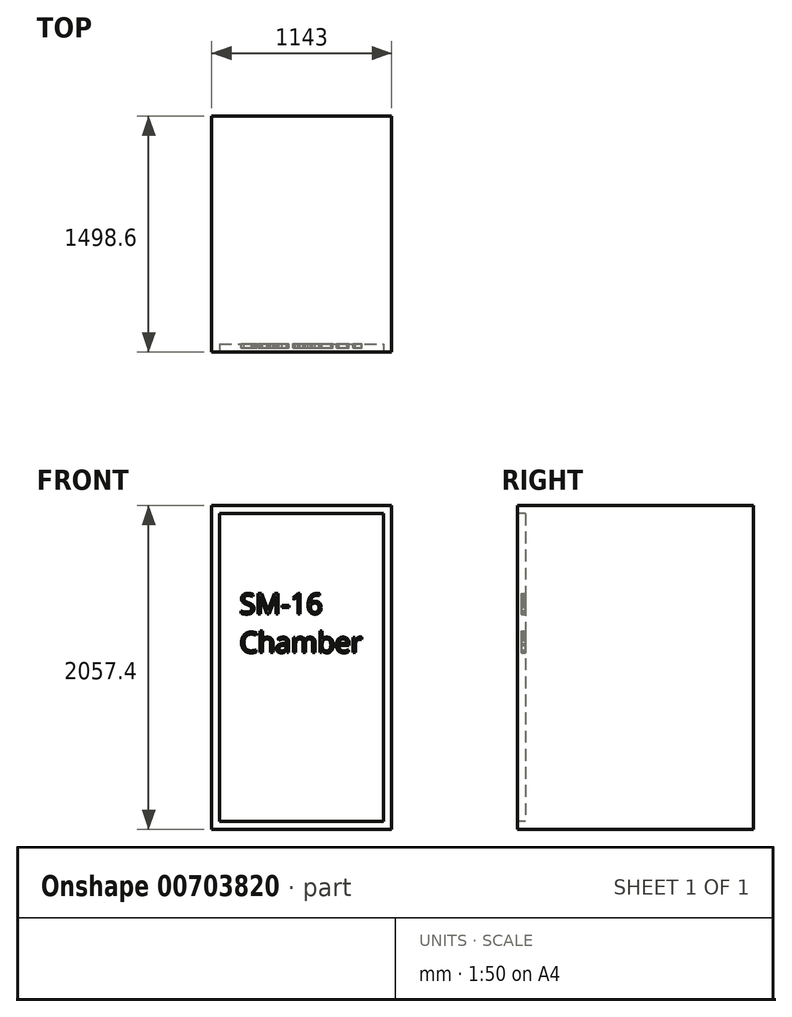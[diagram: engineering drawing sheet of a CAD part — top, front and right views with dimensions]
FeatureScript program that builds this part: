
annotation { "Feature Type Name" : "Feature", "Feature Type Description" : "" }
export const myFeature = defineFeature(function(context is Context, id is Id, definition is map)
    precondition{}
    {
        {
            var Q0;
            Q0=qCreatedBy(makeId("Top.planeOp"),FACE);
            var sketch = newSketch(context, id + "F0", { "sketchPlane" : qUnion([Q0])});
            skLineSegment(sketch, "E0.bottom", {"start": v(571.5, -749.3) * mm, "end": v(-571.5, -749.3) * mm});
            skLineSegment(sketch, "E0.top", {"start": v(571.5, 749.3) * mm, "end": v(-571.5, 749.3) * mm});
            skLineSegment(sketch, "E0.left", {"start": v(571.5, -749.3) * mm, "end": v(571.5, 749.3) * mm});
            skLineSegment(sketch, "E0.right", {"start": v(-571.5, -749.3) * mm, "end": v(-571.5, 749.3) * mm});
            skPoint(sketch, "E0.middle", {"position": v(0, 0) * mm});
            skSolve(sketch);
        }
        {
            var Q0;
            Q0=qSketchRegion(id+"F0",true);
            extrude(context, id + "F1", {"entities" : qUnion([Q0]), "depth" : 2057.4 * mm, "offsetDistance" : 25.4 * mm});
        }
        {
            var Q0;
            Q0=makeQuery(id+"F1.opExtrude","SWEPT_FACE",FACE,{"disambiguationData":[OSD([sQuery(id+"F0.wireOp",EDGE,"E0.bottom")])]});
            var sketch = newSketch(context, id + "F2", { "sketchPlane" : qUnion([Q0])});
            skLineSegment(sketch, "E1.bottom", {"start": v(-520.7, 2006.6) * mm, "end": v(520.7, 2006.6) * mm});
            skLineSegment(sketch, "E1.top", {"start": v(-520.7, 50.8) * mm, "end": v(520.7, 50.8) * mm});
            skLineSegment(sketch, "E1.left", {"start": v(-520.7, 2006.6) * mm, "end": v(-520.7, 50.8) * mm});
            skLineSegment(sketch, "E1.right", {"start": v(520.7, 2006.6) * mm, "end": v(520.7, 50.8) * mm});
            skSolve(sketch);
        }
        {
            var Q0;
            Q0=qSketchRegion(id+"F2",true);
            extrude(context, id + "F3", {"entities" : qUnion([Q0]), "operationType" : NewBodyOperationType.REMOVE, "oppositeDirection" : true, "depth" : 50.8 * mm, "offsetDistance" : 25.4 * mm});
        }
        {
            var Q0;
            Q0=makeQuery(id+"F3.boolean.opBoolean","COPY",FACE,{"derivedFrom":makeQuery(id+"F3.opExtrude","CAP_FACE",FACE,{"disambiguationData":[OSD([sQuery(id+"F2.wireOp",EDGE,"E1.bottom"),sQuery(id+"F2.wireOp",EDGE,"E1.top"),sQuery(id+"F2.wireOp",EDGE,"E1.left"),sQuery(id+"F2.wireOp",EDGE,"E1.right")])],"isStart":false})});
            var sketch = newSketch(context, id + "F4", { "sketchPlane" : qUnion([Q0])});
            skText(sketch, "E2", { "text": "SM-16\nChamber\n", "fontName": "OpenSans-Regular.ttf"});
            const initialGuessF4  = {"E2": [-0.3937, 1.36868, 1, 0, 0.12992]};
            skSetInitialGuess(sketch, initialGuessF4);
            skSolve(sketch);
        }
        {
            var Q0;
            Q0=qSketchRegion(id+"F4",true);
            extrude(context, id + "F5", {"entities" : qUnion([Q0]), "operationType" : NewBodyOperationType.ADD, "depth" : 25.4 * mm, "offsetDistance" : 25.4 * mm});
        }
    });
